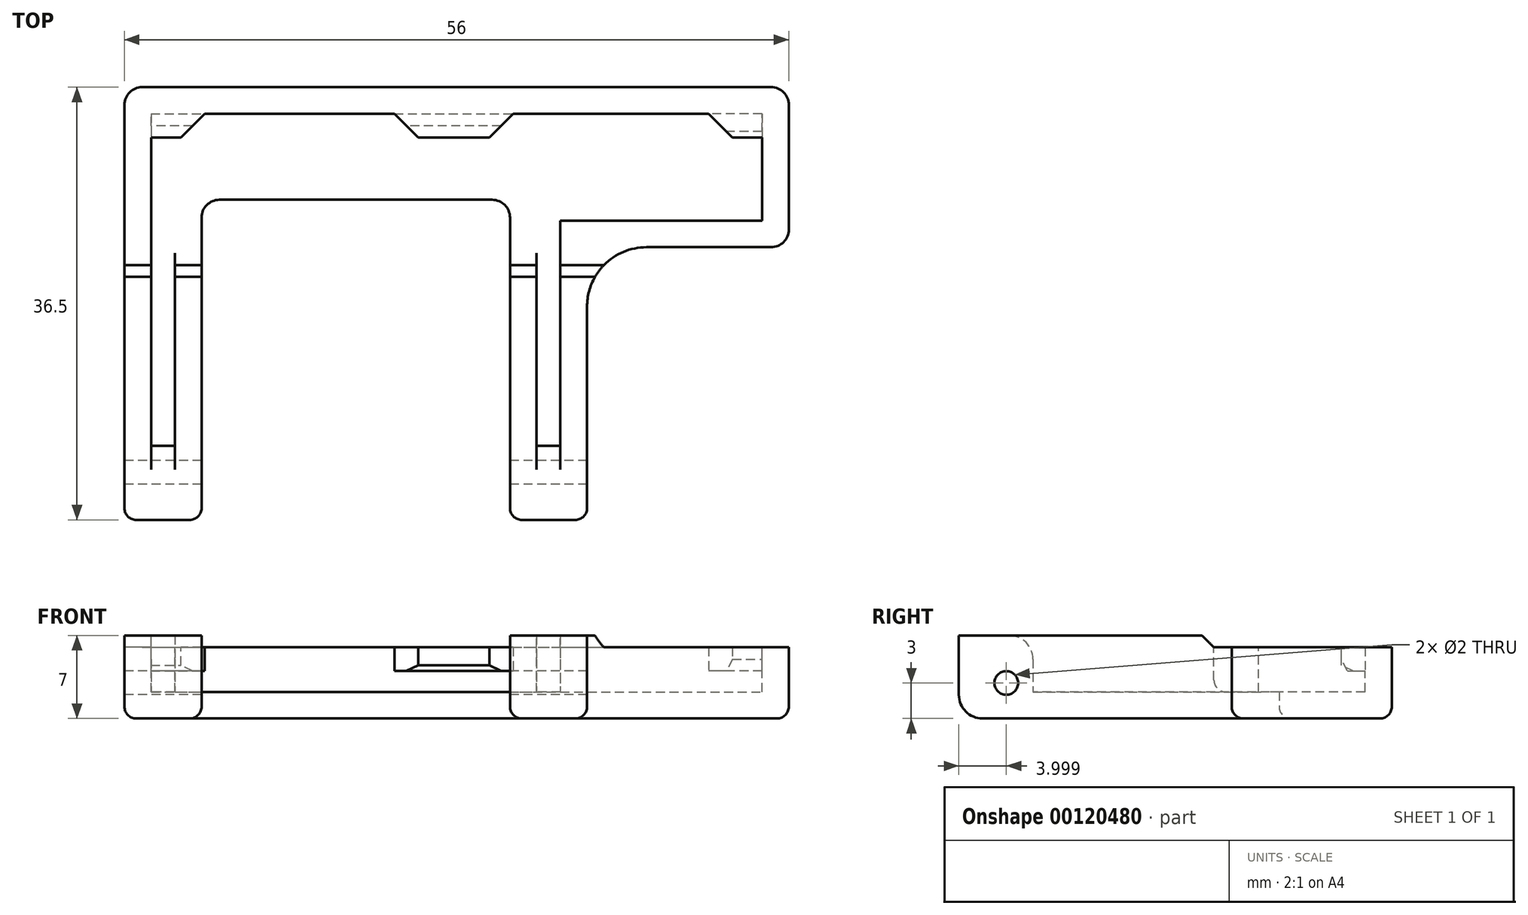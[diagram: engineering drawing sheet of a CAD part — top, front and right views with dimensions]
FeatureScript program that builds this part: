
annotation { "Feature Type Name" : "Feature", "Feature Type Description" : "" }
export const myFeature = defineFeature(function(context is Context, id is Id, definition is map)
    precondition{}
    {
        {
            var Q0;
            Q0=qCreatedBy(makeId("Top.planeOp"),FACE);
            var sketch = newSketch(context, id + "F0", { "sketchPlane" : qUnion([Q0])});
            skLineSegment(sketch, "E0.bottom", {"start": v(-24.35, 17.72) * mm, "end": v(31.65, 17.72) * mm});
            skLineSegment(sketch, "E0.top", {"start": v(-24.35, -18.78) * mm, "end": v(31.65, -18.78) * mm});
            skLineSegment(sketch, "E0.left", {"start": v(-24.35, 17.72) * mm, "end": v(-24.35, -18.78) * mm});
            skLineSegment(sketch, "E0.right", {"start": v(31.65, 17.72) * mm, "end": v(31.65, -18.78) * mm});
            skLineSegment(sketch, "E1.bottom", {"start": v(-17.85, -18.78) * mm, "end": v(8.15, -18.78) * mm});
            skLineSegment(sketch, "E1.top", {"start": v(-17.85, 8.22) * mm, "end": v(8.15, 8.22) * mm});
            skLineSegment(sketch, "E1.left", {"start": v(-17.85, -18.78) * mm, "end": v(-17.85, 8.22) * mm});
            skLineSegment(sketch, "E1.right", {"start": v(8.15, -18.78) * mm, "end": v(8.15, 8.22) * mm});
            skLineSegment(sketch, "E2.bottom", {"start": v(14.65, -18.78) * mm, "end": v(31.65, -18.78) * mm});
            skLineSegment(sketch, "E2.top", {"start": v(14.65, 4.22) * mm, "end": v(31.65, 4.22) * mm});
            skLineSegment(sketch, "E2.left", {"start": v(14.65, -18.78) * mm, "end": v(14.65, 4.22) * mm});
            skLineSegment(sketch, "E2.right", {"start": v(31.65, -18.78) * mm, "end": v(31.65, 4.22) * mm});
            skSolve(sketch);
        }
        {
            var Q0;
            Q0=makeQuery(id+"F0.imprint","IMPRINT",FACE,{"disambiguationData":[TD([[makeQuery(id+"F0.imprint","IMPRINT",EDGE,{"derivedFrom":sQuery(id+"F0.wireOp",EDGE,"E0.bottom")}),-1.0]])]});
            extrude(context, id + "F1", {"entities" : qUnion([Q0]), "depth" : 6 * mm});
        }
        {
            var Q0;
            {var subQ0=sQuery(id+"F0.wireOp",EDGE,"E0.top");Q0=makeQuery(id+"F1.opExtrude","CAP_EDGE",EDGE,{"disambiguationData":[OSD([subQ0]),TDD([makeQuery(id+"F0.imprint","IMPRINT",EDGE,{"disambiguationData":[TD([[makeQuery(id+"F0.imprint","INTERSECT",VERTEX,{"derivedFrom":[subQ0,sQuery(id+"F0.wireOp",EDGE,"E0.left")]}),-1.0]])],"derivedFrom":subQ0})])],"isStart":true});}
            var Q1;
            {var subQ0=sQuery(id+"F0.wireOp",EDGE,"E0.top");Q1=makeQuery(id+"F1.opExtrude","CAP_EDGE",EDGE,{"disambiguationData":[OSD([subQ0]),TDD([makeQuery(id+"F0.imprint","IMPRINT",EDGE,{"disambiguationData":[TD([[makeQuery(id+"F0.imprint","INTERSECT",VERTEX,{"derivedFrom":[subQ0,sQuery(id+"F0.wireOp",EDGE,"E2.bottom"),sQuery(id+"F0.wireOp",EDGE,"E2.left")]}),1.0]])],"derivedFrom":subQ0})])],"isStart":true});}
            fillet(context, id + "F2", {"entities" : qUnion([Q0, Q1]), "radius" : 2 * mm, "tangentPropagation" : true, "allowEdgeOverflow" : false});
        }
        {
            var Q0;
            Q0=makeQuery(id+"F1.opExtrude","SWEPT_EDGE",EDGE,{"disambiguationData":[OSD([sQuery(id+"F0.wireOp",EDGE,"E0.bottom"),sQuery(id+"F0.wireOp",EDGE,"E0.left")])]});
            var Q1;
            Q1=makeQuery(id+"F1.opExtrude","SWEPT_EDGE",EDGE,{"disambiguationData":[OSD([sQuery(id+"F0.wireOp",EDGE,"E0.bottom"),sQuery(id+"F0.wireOp",EDGE,"E0.right")])]});
            var Q2;
            Q2=makeQuery(id+"F1.opExtrude","SWEPT_EDGE",EDGE,{"disambiguationData":[OSD([sQuery(id+"F0.wireOp",EDGE,"E0.right"),sQuery(id+"F0.wireOp",EDGE,"E2.top"),sQuery(id+"F0.wireOp",EDGE,"E2.right")])]});
            var Q3;
            Q3=makeQuery(id+"F1.opExtrude","SWEPT_EDGE",EDGE,{"disambiguationData":[OSD([sQuery(id+"F0.wireOp",EDGE,"E1.top"),sQuery(id+"F0.wireOp",EDGE,"E1.right")])]});
            var Q4;
            Q4=makeQuery(id+"F1.opExtrude","SWEPT_EDGE",EDGE,{"disambiguationData":[OSD([sQuery(id+"F0.wireOp",EDGE,"E1.top"),sQuery(id+"F0.wireOp",EDGE,"E1.left")])]});
            fillet(context, id + "F3", {"entities" : qUnion([Q0, Q1, Q2, Q3, Q4]), "radius" : 1.5 * mm, "tangentPropagation" : true, "allowEdgeOverflow" : false});
        }
        {
            var Q0;
            Q0=makeQuery(id+"F1.opExtrude","CAP_FACE",FACE,{"disambiguationData":[OSD([sQuery(id+"F0.wireOp",EDGE,"E0.bottom"),sQuery(id+"F0.wireOp",EDGE,"E0.top"),sQuery(id+"F0.wireOp",EDGE,"E0.left"),sQuery(id+"F0.wireOp",EDGE,"E0.right"),sQuery(id+"F0.wireOp",EDGE,"E1.top"),sQuery(id+"F0.wireOp",EDGE,"E1.left"),sQuery(id+"F0.wireOp",EDGE,"E1.right"),sQuery(id+"F0.wireOp",EDGE,"E2.top"),sQuery(id+"F0.wireOp",EDGE,"E2.left")])],"isStart":false});
            shell(context, id + "F4", {"entities" : qUnion([Q0]), "thickness" : 2.25 * mm});
        }
        {
            var Q0;
            Q0=makeQuery(id+"F4.opShell","OFFSET_FACE",FACE,{"disambiguationData":[OSD([sQuery(id+"F0.wireOp",EDGE,"E0.bottom")])]});
            var sketch = newSketch(context, id + "F5", { "sketchPlane" : qUnion([Q0])});
            skLineSegment(sketch, "E3.bottom", {"start": v(-22.1, 6) * mm, "end": v(-17.6, 6) * mm});
            skLineSegment(sketch, "E3.top", {"start": v(-22.1, 4) * mm, "end": v(-17.6, 4) * mm});
            skLineSegment(sketch, "E3.left", {"start": v(-22.1, 6) * mm, "end": v(-22.1, 4) * mm});
            skLineSegment(sketch, "E3.right", {"start": v(-17.6, 6) * mm, "end": v(-17.6, 4) * mm});
            skLineSegment(sketch, "E4.bottom", {"start": v(-1.6, 6) * mm, "end": v(8.4, 6) * mm});
            skLineSegment(sketch, "E4.top", {"start": v(-1.6, 4) * mm, "end": v(8.4, 4) * mm});
            skLineSegment(sketch, "E4.left", {"start": v(-1.6, 6) * mm, "end": v(-1.6, 4) * mm});
            skLineSegment(sketch, "E4.right", {"start": v(8.4, 6) * mm, "end": v(8.4, 4) * mm});
            skLineSegment(sketch, "E5.bottom", {"start": v(29.4, 6) * mm, "end": v(24.9, 6) * mm});
            skLineSegment(sketch, "E5.top", {"start": v(29.4, 4) * mm, "end": v(24.9, 4) * mm});
            skLineSegment(sketch, "E5.left", {"start": v(29.4, 6) * mm, "end": v(29.4, 4) * mm});
            skLineSegment(sketch, "E5.right", {"start": v(24.9, 6) * mm, "end": v(24.9, 4) * mm});
            skSolve(sketch);
        }
        {
            var Q0;
            Q0=makeQuery(id+"F5.imprint","IMPRINT",FACE,{"disambiguationData":[TD([[makeQuery(id+"F5.imprint","IMPRINT",EDGE,{"derivedFrom":sQuery(id+"F5.wireOp",EDGE,"E3.bottom")}),-1.0]])]});
            var Q1;
            Q1=makeQuery(id+"F5.imprint","IMPRINT",FACE,{"disambiguationData":[TD([[makeQuery(id+"F5.imprint","IMPRINT",EDGE,{"derivedFrom":sQuery(id+"F5.wireOp",EDGE,"E4.bottom")}),-1.0]])]});
            var Q2;
            Q2=makeQuery(id+"F5.imprint","IMPRINT",FACE,{"disambiguationData":[TD([[makeQuery(id+"F5.imprint","IMPRINT",EDGE,{"derivedFrom":sQuery(id+"F5.wireOp",EDGE,"E5.bottom")}),-1.0]])]});
            extrude(context, id + "F6", {"entities" : qUnion([Q0, Q1, Q2]), "operationType" : NewBodyOperationType.ADD, "depth" : 2 * mm});
        }
        {
            var Q0;
            Q0=makeQuery(id+"F6.opExtrude","CAP_EDGE",EDGE,{"disambiguationData":[OSD([sQuery(id+"F5.wireOp",EDGE,"E3.right")])],"isStart":false});
            var Q1;
            Q1=makeQuery(id+"F6.opExtrude","CAP_EDGE",EDGE,{"disambiguationData":[OSD([sQuery(id+"F5.wireOp",EDGE,"E4.left")])],"isStart":false});
            var Q2;
            Q2=makeQuery(id+"F6.opExtrude","CAP_EDGE",EDGE,{"disambiguationData":[OSD([sQuery(id+"F5.wireOp",EDGE,"E4.right")])],"isStart":false});
            var Q3;
            Q3=makeQuery(id+"F6.opExtrude","CAP_EDGE",EDGE,{"disambiguationData":[OSD([sQuery(id+"F5.wireOp",EDGE,"E5.right")])],"isStart":false});
            chamfer(context, id + "F7", {"entities" : qUnion([Q0, Q1, Q2, Q3]), "width" : 2 * mm, "tangentPropagation" : true});
        }
        {
            var Q0;
            {var subQ0=sQuery(id+"F0.wireOp",EDGE,"E0.top");var subQ1=makeQuery(id+"F0.imprint","IMPRINT",EDGE,{"disambiguationData":[TD([[makeQuery(id+"F0.imprint","INTERSECT",VERTEX,{"derivedFrom":[subQ0,sQuery(id+"F0.wireOp",EDGE,"E0.left")]}),-1.0]])],"derivedFrom":subQ0});Q0=makeQuery(id+"F16.boolean.opBoolean","MERGE",FACE,{"derivedFrom":[makeQuery(id+"F4.opShell","OFFSET_FACE",FACE,{"disambiguationData":[OSD([subQ0]),TDD([makeQuery(id+"F1.opExtrude","SWEPT_FACE",FACE,{"disambiguationData":[OSD([subQ0]),TDD([subQ1])]})])]}),makeQuery(id+"F16.opExtrude","SWEPT_FACE",FACE,{"disambiguationData":[OSD([subQ0]),TDD([makeQuery(id+"F15.imprint","IMPRINT",EDGE,{"derivedFrom":makeQuery(id+"F4.opShell","OFFSET_EDGE",EDGE,{"disambiguationData":[OSD([subQ0]),TDD([makeQuery(id+"F1.opExtrude","CAP_EDGE",EDGE,{"disambiguationData":[OSD([subQ0]),TDD([subQ1])],"isStart":false})])]})})])]})]});}
            var Q1;
            {var subQ0=sQuery(id+"F0.wireOp",EDGE,"E0.top");var subQ1=makeQuery(id+"F0.imprint","IMPRINT",EDGE,{"disambiguationData":[TD([[makeQuery(id+"F0.imprint","INTERSECT",VERTEX,{"derivedFrom":[subQ0,sQuery(id+"F0.wireOp",EDGE,"E2.bottom"),sQuery(id+"F0.wireOp",EDGE,"E2.left")]}),1.0]])],"derivedFrom":subQ0});Q1=makeQuery(id+"F16.boolean.opBoolean","MERGE",FACE,{"derivedFrom":[makeQuery(id+"F4.opShell","OFFSET_FACE",FACE,{"disambiguationData":[OSD([subQ0]),TDD([makeQuery(id+"F1.opExtrude","SWEPT_FACE",FACE,{"disambiguationData":[OSD([subQ0]),TDD([subQ1])]})])]}),makeQuery(id+"F16.opExtrude","SWEPT_FACE",FACE,{"disambiguationData":[OSD([subQ0]),TDD([makeQuery(id+"F15.imprint","IMPRINT",EDGE,{"derivedFrom":makeQuery(id+"F4.opShell","OFFSET_EDGE",EDGE,{"disambiguationData":[OSD([subQ0]),TDD([makeQuery(id+"F1.opExtrude","CAP_EDGE",EDGE,{"disambiguationData":[OSD([subQ0]),TDD([subQ1])],"isStart":false})])]})})])]})]});}
            extrude(context, id + "F8", {"entities" : qUnion([Q0, Q1]), "operationType" : NewBodyOperationType.ADD, "depth" : 4 * mm});
        }
        {
            var Q0;
            Q0=makeQuery(id+"F1.opExtrude","SWEPT_FACE",FACE,{"disambiguationData":[OSD([sQuery(id+"F0.wireOp",EDGE,"E0.left")])]});
            var sketch = newSketch(context, id + "F9", { "sketchPlane" : qUnion([Q0])});
            skCircle(sketch, "E6", {"center": v(14.78, 3) * mm, "radius": 1 * mm});
            skSolve(sketch);
        }
        {
            var Q0;
            Q0=makeQuery(id+"F9.imprint","IMPRINT",FACE,{"disambiguationData":[TD([[makeQuery(id+"F9.imprint","IMPRINT",EDGE,{"derivedFrom":sQuery(id+"F9.wireOp",EDGE,"E6")}),1.0]])]});
            var Q1;
            Q1=makeQuery(id+"F9.imprint","IMPRINT",FACE,{"disambiguationData":[TD([[makeQuery(id+"F9.imprint","IMPRINT",EDGE,{"derivedFrom":sQuery(id+"F9.wireOp",EDGE,"E6")}),1.0]])]});
            extrude(context, id + "F10", {"entities" : qUnion([Q0, Q1]), "operationType" : NewBodyOperationType.REMOVE, "endBound" : BoundingType.THROUGH_ALL, "oppositeDirection" : true, "depth" : 25 * mm});
        }
        {
            var Q0;
            Q0=makeQuery(id+"F6.boolean.opBoolean","MERGE",FACE,{"derivedFrom":[makeQuery(id+"F1.opExtrude","CAP_FACE",FACE,{"disambiguationData":[OSD([sQuery(id+"F0.wireOp",EDGE,"E0.bottom"),sQuery(id+"F0.wireOp",EDGE,"E0.top"),sQuery(id+"F0.wireOp",EDGE,"E0.left"),sQuery(id+"F0.wireOp",EDGE,"E0.right"),sQuery(id+"F0.wireOp",EDGE,"E1.top"),sQuery(id+"F0.wireOp",EDGE,"E1.left"),sQuery(id+"F0.wireOp",EDGE,"E1.right"),sQuery(id+"F0.wireOp",EDGE,"E2.top"),sQuery(id+"F0.wireOp",EDGE,"E2.left")])],"isStart":false}),makeQuery(id+"F6.opExtrude","SWEPT_FACE",FACE,{"disambiguationData":[OSD([sQuery(id+"F5.wireOp",EDGE,"E3.bottom")])]}),makeQuery(id+"F6.opExtrude","SWEPT_FACE",FACE,{"disambiguationData":[OSD([sQuery(id+"F5.wireOp",EDGE,"E4.bottom")])]}),makeQuery(id+"F6.opExtrude","SWEPT_FACE",FACE,{"disambiguationData":[OSD([sQuery(id+"F5.wireOp",EDGE,"E5.bottom")])]})]});
            var sketch = newSketch(context, id + "F11", { "sketchPlane" : qUnion([Q0])});
            skLineSegment(sketch, "E7.bottom", {"start": v(-20.1, 2.72) * mm, "end": v(10.4, 2.72) * mm});
            skLineSegment(sketch, "E7.top", {"start": v(-20.1, 10.98) * mm, "end": v(10.4, 10.98) * mm});
            skLineSegment(sketch, "E7.left", {"start": v(-20.1, 2.72) * mm, "end": v(-20.1, 10.98) * mm});
            skLineSegment(sketch, "E7.right", {"start": v(10.4, 2.72) * mm, "end": v(10.4, 10.98) * mm});
            skSolve(sketch);
        }
        {
            var Q0;
            {var subQ0=sQuery(id+"F0.wireOp",EDGE,"E1.top");var subQ1=makeQuery(id+"F1.opExtrude","CAP_EDGE",EDGE,{"disambiguationData":[OSD([subQ0])],"isStart":false});Q0=makeQuery(id+"F11.imprint","IMPRINT",FACE,{"disambiguationData":[TD([[makeQuery(id+"F11.imprint","IMPRINT",EDGE,{"derivedFrom":subQ1}),1.0]])]});}
            extrude(context, id + "F12", {"entities" : qUnion([Q0]), "operationType" : NewBodyOperationType.REMOVE, "oppositeDirection" : true, "depth" : 3.75 * mm});
        }
        {
            var Q0;
            {var subQ0=sQuery(id+"F11.wireOp",EDGE,"E7.bottom");var subQ1=sQuery(id+"F0.wireOp",EDGE,"E1.left");var subQ2=makeQuery(id+"F1.opExtrude","CAP_EDGE",EDGE,{"disambiguationData":[OSD([subQ1])],"isStart":false});Q0=makeQuery(id+"F12.boolean.opBoolean","COPY",EDGE,{"derivedFrom":makeQuery(id+"F12.opExtrude","CAP_EDGE",EDGE,{"disambiguationData":[OSD([subQ0]),TDD([makeQuery(id+"F11.imprint","IMPRINT",EDGE,{"disambiguationData":[TD([[makeQuery(id+"F11.imprint","INTERSECT",VERTEX,{"derivedFrom":[subQ2,subQ0]}),1.0]])],"derivedFrom":subQ0})])],"isStart":false})});}
            var Q1;
            {var subQ0=sQuery(id+"F11.wireOp",EDGE,"E7.bottom");var subQ1=sQuery(id+"F0.wireOp",EDGE,"E1.right");var subQ2=makeQuery(id+"F1.opExtrude","CAP_EDGE",EDGE,{"disambiguationData":[OSD([subQ1])],"isStart":false});Q1=makeQuery(id+"F12.boolean.opBoolean","COPY",EDGE,{"derivedFrom":makeQuery(id+"F12.opExtrude","CAP_EDGE",EDGE,{"disambiguationData":[OSD([subQ0]),TDD([makeQuery(id+"F11.imprint","IMPRINT",EDGE,{"disambiguationData":[TD([[makeQuery(id+"F11.imprint","INTERSECT",VERTEX,{"derivedFrom":[subQ2,subQ0]}),-1.0]])],"derivedFrom":subQ0})])],"isStart":false})});}
            fillet(context, id + "F13", {"entities" : qUnion([Q0, Q1]), "radius" : 1 * mm, "tangentPropagation" : true, "allowEdgeOverflow" : false});
        }
        {
            var Q0;
            Q0=makeQuery(id+"F6.opExtrude","CAP_EDGE",EDGE,{"disambiguationData":[OSD([sQuery(id+"F5.wireOp",EDGE,"E4.top")])],"isStart":false});
            var Q1;
            Q1=makeQuery(id+"F6.opExtrude","CAP_EDGE",EDGE,{"disambiguationData":[OSD([sQuery(id+"F5.wireOp",EDGE,"E5.top")])],"isStart":false});
            var Q2;
            Q2=makeQuery(id+"F6.opExtrude","CAP_EDGE",EDGE,{"disambiguationData":[OSD([sQuery(id+"F5.wireOp",EDGE,"E3.top")])],"isStart":false});
            chamfer(context, id + "F14", {"entities" : qUnion([Q0, Q1, Q2]), "chamferType" : ChamferType.TWO_OFFSETS, "width1" : 0.5 * mm, "oppositeDirection" : false, "width2" : 1 * mm, "tangentPropagation" : true});
        }
        {
            var Q0;
            Q0=makeQuery(id+"F6.boolean.opBoolean","MERGE",FACE,{"derivedFrom":[makeQuery(id+"F1.opExtrude","CAP_FACE",FACE,{"disambiguationData":[OSD([sQuery(id+"F0.wireOp",EDGE,"E0.bottom"),sQuery(id+"F0.wireOp",EDGE,"E0.top"),sQuery(id+"F0.wireOp",EDGE,"E0.left"),sQuery(id+"F0.wireOp",EDGE,"E0.right"),sQuery(id+"F0.wireOp",EDGE,"E1.top"),sQuery(id+"F0.wireOp",EDGE,"E1.left"),sQuery(id+"F0.wireOp",EDGE,"E1.right"),sQuery(id+"F0.wireOp",EDGE,"E2.top"),sQuery(id+"F0.wireOp",EDGE,"E2.left")])],"isStart":false}),makeQuery(id+"F6.opExtrude","SWEPT_FACE",FACE,{"disambiguationData":[OSD([sQuery(id+"F5.wireOp",EDGE,"E3.bottom")])]}),makeQuery(id+"F6.opExtrude","SWEPT_FACE",FACE,{"disambiguationData":[OSD([sQuery(id+"F5.wireOp",EDGE,"E4.bottom")])]}),makeQuery(id+"F6.opExtrude","SWEPT_FACE",FACE,{"disambiguationData":[OSD([sQuery(id+"F5.wireOp",EDGE,"E5.bottom")])]})]});
            var sketch = newSketch(context, id + "F15", { "sketchPlane" : qUnion([Q0])});
            skLineSegment(sketch, "E8.bottom", {"start": v(-17.85, 2.72) * mm, "end": v(-24.35, 2.72) * mm});
            skLineSegment(sketch, "E8.top", {"start": v(-17.85, -20.88) * mm, "end": v(-24.35, -20.88) * mm});
            skLineSegment(sketch, "E8.left", {"start": v(-17.85, 2.72) * mm, "end": v(-17.85, -20.88) * mm});
            skLineSegment(sketch, "E8.right", {"start": v(-24.35, 2.72) * mm, "end": v(-24.35, -20.88) * mm});
            skLineSegment(sketch, "E9.bottom", {"start": v(8.15, 2.72) * mm, "end": v(14.65, 2.72) * mm});
            skLineSegment(sketch, "E9.top", {"start": v(8.15, -20.72) * mm, "end": v(14.65, -20.72) * mm});
            skLineSegment(sketch, "E9.left", {"start": v(8.15, 2.72) * mm, "end": v(8.15, -20.72) * mm});
            skLineSegment(sketch, "E9.right", {"start": v(14.65, 2.72) * mm, "end": v(14.65, -20.72) * mm});
            skSolve(sketch);
        }
        {
            var Q0;
            {var subQ1=sQuery(id+"F0.wireOp",EDGE,"E1.left");var subQ15=makeQuery(id+"F4.opShell","OFFSET_EDGE",EDGE,{"disambiguationData":[OSD([subQ1]),TDD([makeQuery(id+"F1.opExtrude","CAP_EDGE",EDGE,{"disambiguationData":[OSD([subQ1])],"isStart":false})])]});Q0=makeQuery(id+"F15.imprint","IMPRINT",FACE,{"disambiguationData":[TD([[makeQuery(id+"F15.imprint","IMPRINT",EDGE,{"derivedFrom":subQ15}),-1.0]])]});}
            var Q1;
            {var subQ2=sQuery(id+"F0.wireOp",EDGE,"E1.right");var subQ16=makeQuery(id+"F4.opShell","OFFSET_EDGE",EDGE,{"disambiguationData":[OSD([subQ2]),TDD([makeQuery(id+"F1.opExtrude","CAP_EDGE",EDGE,{"disambiguationData":[OSD([subQ2])],"isStart":false})])]});Q1=makeQuery(id+"F15.imprint","IMPRINT",FACE,{"disambiguationData":[TD([[makeQuery(id+"F15.imprint","IMPRINT",EDGE,{"derivedFrom":subQ16}),1.0]])]});}
            extrude(context, id + "F16", {"entities" : qUnion([Q0, Q1]), "operationType" : NewBodyOperationType.ADD, "depth" : 1 * mm});
        }
        {
            var Q0;
            {var subQ0=sQuery(id+"F15.wireOp",EDGE,"E8.bottom");var subQ1=sQuery(id+"F0.wireOp",EDGE,"E0.left");var subQ2=makeQuery(id+"F1.opExtrude","CAP_EDGE",EDGE,{"disambiguationData":[OSD([subQ1])],"isStart":false});Q0=makeQuery(id+"F16.opExtrude","CAP_EDGE",EDGE,{"disambiguationData":[OSD([subQ0]),TDD([makeQuery(id+"F15.imprint","IMPRINT",EDGE,{"disambiguationData":[TD([[makeQuery(id+"F15.imprint","INTERSECT",VERTEX,{"derivedFrom":[makeQuery(id+"F4.opShell","OFFSET_EDGE",EDGE,{"disambiguationData":[OSD([subQ1]),TDD([subQ2])]}),subQ0]}),-1.0]])],"derivedFrom":subQ0})])],"isStart":false});}
            var Q1;
            {var subQ0=sQuery(id+"F15.wireOp",EDGE,"E8.bottom");Q1=makeQuery(id+"F16.opExtrude","CAP_EDGE",EDGE,{"disambiguationData":[OSD([subQ0]),TDD([makeQuery(id+"F15.imprint","IMPRINT",EDGE,{"disambiguationData":[TD([[makeQuery(id+"F15.imprint","INTERSECT",VERTEX,{"derivedFrom":[subQ0,sQuery(id+"F15.wireOp",EDGE,"E8.left")]}),1.0]])],"derivedFrom":subQ0})])],"isStart":false});}
            var Q2;
            {var subQ0=sQuery(id+"F15.wireOp",EDGE,"E9.bottom");Q2=makeQuery(id+"F16.opExtrude","CAP_EDGE",EDGE,{"disambiguationData":[OSD([subQ0]),TDD([makeQuery(id+"F15.imprint","IMPRINT",EDGE,{"disambiguationData":[TD([[makeQuery(id+"F15.imprint","INTERSECT",VERTEX,{"derivedFrom":[subQ0,sQuery(id+"F15.wireOp",EDGE,"E9.left")]}),-1.0]])],"derivedFrom":subQ0})])],"isStart":false});}
            var Q3;
            {var subQ0=sQuery(id+"F15.wireOp",EDGE,"E9.bottom");Q3=makeQuery(id+"F16.opExtrude","CAP_EDGE",EDGE,{"disambiguationData":[OSD([subQ0]),TDD([makeQuery(id+"F15.imprint","IMPRINT",EDGE,{"disambiguationData":[TD([[makeQuery(id+"F15.imprint","INTERSECT",VERTEX,{"derivedFrom":[subQ0,sQuery(id+"F15.wireOp",EDGE,"E9.right")]}),1.0]])],"derivedFrom":subQ0})])],"isStart":false});}
            chamfer(context, id + "F17", {"entities" : qUnion([Q0, Q1, Q2, Q3]), "width" : 1 * mm, "tangentPropagation" : true});
        }
        {
            var Q0;
            {var subQ0=sQuery(id+"F0.wireOp",EDGE,"E0.top");Q0=makeQuery(id+"F16.opExtrude","CAP_EDGE",EDGE,{"disambiguationData":[OSD([subQ0]),TDD([makeQuery(id+"F15.imprint","IMPRINT",EDGE,{"derivedFrom":makeQuery(id+"F8.opExtrude","CAP_EDGE",EDGE,{"disambiguationData":[OSD([subQ0]),TDD([makeQuery(id+"F4.opShell","OFFSET_EDGE",EDGE,{"disambiguationData":[OSD([subQ0]),TDD([makeQuery(id+"F1.opExtrude","CAP_EDGE",EDGE,{"disambiguationData":[OSD([subQ0]),TDD([makeQuery(id+"F0.imprint","IMPRINT",EDGE,{"disambiguationData":[TD([[makeQuery(id+"F0.imprint","INTERSECT",VERTEX,{"derivedFrom":[subQ0,sQuery(id+"F0.wireOp",EDGE,"E2.bottom"),sQuery(id+"F0.wireOp",EDGE,"E2.left")]}),1.0]])],"derivedFrom":subQ0})])],"isStart":false})])]})])],"isStart":false})})])],"isStart":false});}
            var Q1;
            {var subQ0=sQuery(id+"F0.wireOp",EDGE,"E0.top");Q1=makeQuery(id+"F16.opExtrude","CAP_EDGE",EDGE,{"disambiguationData":[OSD([subQ0]),TDD([makeQuery(id+"F15.imprint","IMPRINT",EDGE,{"derivedFrom":makeQuery(id+"F8.opExtrude","CAP_EDGE",EDGE,{"disambiguationData":[OSD([subQ0]),TDD([makeQuery(id+"F4.opShell","OFFSET_EDGE",EDGE,{"disambiguationData":[OSD([subQ0]),TDD([makeQuery(id+"F1.opExtrude","CAP_EDGE",EDGE,{"disambiguationData":[OSD([subQ0]),TDD([makeQuery(id+"F0.imprint","IMPRINT",EDGE,{"disambiguationData":[TD([[makeQuery(id+"F0.imprint","INTERSECT",VERTEX,{"derivedFrom":[subQ0,sQuery(id+"F0.wireOp",EDGE,"E0.left")]}),-1.0]])],"derivedFrom":subQ0})])],"isStart":false})])]})])],"isStart":false})})])],"isStart":false});}
            fillet(context, id + "F18", {"entities" : qUnion([Q0, Q1]), "radius" : 2 * mm, "tangentPropagation" : true, "allowEdgeOverflow" : false});
        }
        {
            var Q0;
            Q0=makeQuery(id+"F1.opExtrude","SWEPT_EDGE",EDGE,{"disambiguationData":[OSD([sQuery(id+"F0.wireOp",EDGE,"E2.top"),sQuery(id+"F0.wireOp",EDGE,"E2.left")])]});
            fillet(context, id + "F19", {"entities" : qUnion([Q0]), "radius" : 5 * mm, "tangentPropagation" : true, "allowEdgeOverflow" : false});
        }
        {
            var Q0;
            Q0=makeQuery(id+"F1.opExtrude","CAP_EDGE",EDGE,{"disambiguationData":[OSD([sQuery(id+"F0.wireOp",EDGE,"E0.right")])],"isStart":true});
            var Q1;
            Q1=makeQuery(id+"F1.opExtrude","CAP_EDGE",EDGE,{"disambiguationData":[OSD([sQuery(id+"F0.wireOp",EDGE,"E1.top")])],"isStart":true});
            fillet(context, id + "F20", {"entities" : qUnion([Q0, Q1]), "radius" : 1 * mm, "tangentPropagation" : true, "allowEdgeOverflow" : false});
        }
    });
